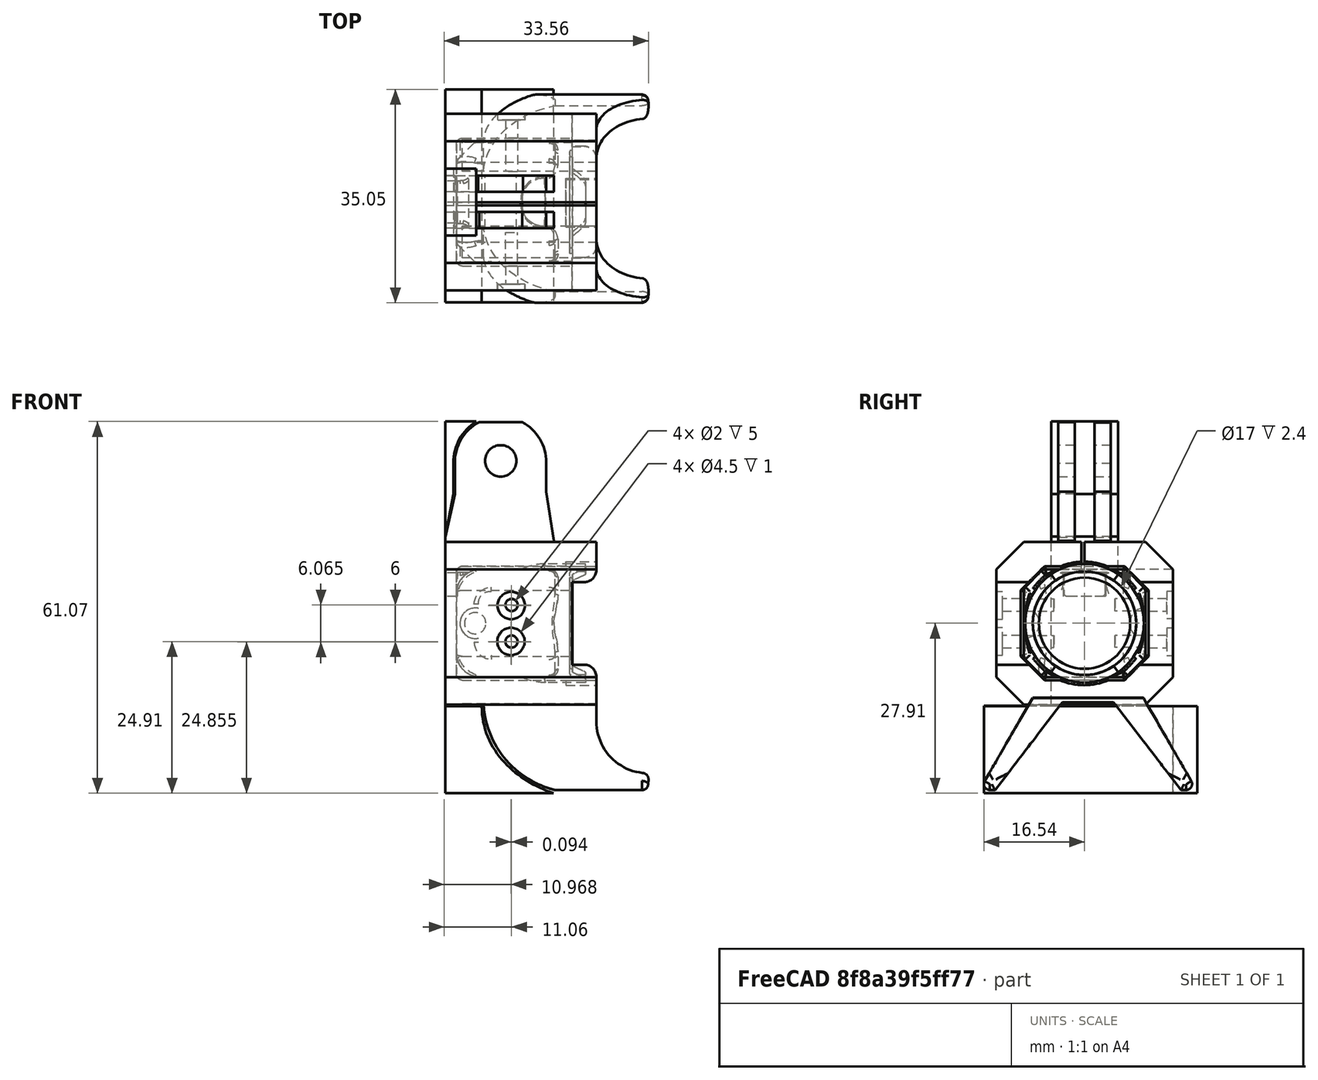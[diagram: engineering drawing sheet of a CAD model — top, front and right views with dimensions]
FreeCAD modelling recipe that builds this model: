
FCSTD DOCUMENT  (FreeCAD 0.19R24267 +99 (Git))
Label: O3头
License: All rights reserved
LicenseURL: http://en.wikipedia.org/wiki/All_rights_reserved
objects: Sketcher::SketchObject×22, PartDesign::Pocket×16, PartDesign::Pad×7, PartDesign::Fillet×5, Mesh::Feature×4, Part::Feature×1, PartDesign::Chamfer×1, PartDesign::Hole×1, PartDesign::Body×1
note: 84 computed .brp shape members not serialized (recipe doc carries the construction recipe); baked Part::Feature solids carry a one-line shape summary decoded from their .brp

FEATURE [Part::Feature] Solid  label="DJI_O3_CAM v1"
  shape: bbox 22.46 x 20.3 x 19.67 mm, 153 faces (baked)
FEATURE [Sketcher::SketchObject] Sketch
  FullyConstrained = false
  MapMode = 5
  Placement = pos=(0,0,0) rot=(0.57735,0.57735,0.57735;2.0944rad)
  Support = -> [YZ_Plane]
  sketch-geometry (18):
    g0: LineSegment StartX=-0.5 StartY=14.2836 StartZ=0 EndX=3.43199 EndY=18.2213 EndZ=0
    g1: LineSegment StartX=3.43199 StartY=18.2213 StartZ=0 EndX=16.5779 EndY=18.2213 EndZ=0
    g2: LineSegment StartX=16.5779 StartY=18.2213 StartZ=0 EndX=20.5092 EndY=14.283 EndZ=0
    g3: LineSegment StartX=20.5092 StartY=14.283 StartZ=0 EndX=20.5092 EndY=3.43765 EndZ=0
    g4: LineSegment StartX=20.5092 StartY=3.43765 StartZ=0 EndX=16.5772 EndY=-0.5 EndZ=0
    g5: LineSegment StartX=16.5772 StartY=-0.5 StartZ=0 EndX=3.43136 EndY=-0.5 EndZ=0
    g6: LineSegment StartX=3.43136 StartY=-0.5 StartZ=0 EndX=-0.5 EndY=3.43828 EndZ=0
    g7: LineSegment StartX=-0.5 StartY=3.43828 StartZ=0 EndX=-0.5 EndY=14.2836 EndZ=0
    g8: LineSegment StartX=0.297912 StartY=2.88402 StartZ=0 EndX=2.88412 EndY=0.293255 EndZ=0
    g9: LineSegment StartX=19.6882 StartY=2.88174 StartZ=0 EndX=17.0961 EndY=0.285953 EndZ=0
    g10: LineSegment StartX=3.7151 StartY=17.7213 StartZ=0 EndX=5.2908 EndY=17.7213 EndZ=0
    g11: LineSegment StartX=3.91307 StartY=0 StartZ=0 EndX=4.96058 EndY=0 EndZ=0
    g12: LineSegment StartX=20.0092 StartY=5.92573 StartZ=0 EndX=20.0092 EndY=3.95872 EndZ=0
    g13: LineSegment StartX=18.612 StartY=15.9146 StartZ=0 EndX=19.1853 EndY=15.3357 EndZ=0
    g14: LineSegment StartX=-4.5 StartY=22.2213 StartZ=0 EndX=24.5092 EndY=22.2213 EndZ=0
    g15: LineSegment StartX=24.5092 StartY=22.2213 StartZ=0 EndX=24.5092 EndY=-4.5 EndZ=0
    g16: LineSegment StartX=24.5092 StartY=-4.5 StartZ=0 EndX=-4.5 EndY=-4.5 EndZ=0
    g17: LineSegment StartX=-4.5 StartY=-4.5 StartZ=0 EndX=-4.5 EndY=22.2213 EndZ=0
  constraints (55):
    c: Coincident(g0,g1)
    c: Horizontal(g1)
    c: Coincident(g1,g2)
    c: Coincident(g2,g3)
    c: Vertical(g3)
    c: Coincident(g3,g4)
    c: Coincident(g4,g5)
    c: Horizontal(g5)
    c: Coincident(g5,g6)
    c: Coincident(g6,g7)
    c: Vertical(g7)
    c: Parallel(g4,g0)
    c: Parallel(g2,g6)
    c: Equal(g1,g5)
    c: Equal(g7,g3)
    c: Equal(g0,g2)
    c: Coincident(g7,g0)
    c: DistanceX(g8) = 0.297912
    c: DistanceY(g8) = 2.88402
    c: DistanceX(g8) = 2.88412
    c: DistanceY(g8) = 0.293255
    c: Parallel(g8,g6)
    c: DistanceX(g9,g9) = -2.59206
    c: DistanceY(g9,g9) = -2.59578
    c: Parallel(g4,g9)
    c: DistanceX(g-2,g0) = -0.5
    c: Horizontal(g10)
    c: DistanceX(g10,g10) = 1.5757
    c: DistanceX(g10) = 3.7151
    c: DistanceY(g10) = 17.7213
    c: PointOnObject(g11,g-1)
    c: PointOnObject(g11,g-1)
    c: Distance(g5,g11) = 0.5
    c: Vertical(g12)
    c: DistanceX(g12) = 20.0092
    c: DistanceY(g12) = 3.95872
    c: Distance(g3,g12) = 0.5
    c: DistanceX(g13,g13) = 0.573332
    c: DistanceY(g13,g13) = -0.578954
    c: Distance(g2,g13) = 0.2
    c: DistanceX(g13) = 19.1853
    c: DistanceY(g13) = 15.3357
    c: Coincident(g14,g15)
    c: Coincident(g15,g16)
    c: Coincident(g16,g17)
    c: Coincident(g17,g14)
    c: Horizontal(g14)
    c: Horizontal(g16)
    c: Vertical(g15)
    c: Vertical(g17)
    c: Distance(g2,g15) = 4
    c: Distance(g0,g17) = 4
    c: Distance(g0,g10) = 0.5
    c: Distance(g14,g1) = 4
    c: Distance(g15,g5) = 4
FEATURE [PartDesign::Pad] Pad
  Direction = (1,1,1)
  Length = 23
  Length2 = 100
  Placement = pos=(0,0,0) rot=(0.57735,0.57735,0.57735;2.0944rad)
  Profile = -> Sketch
  Type = 0
FEATURE [Sketcher::SketchObject] Sketch001
  ExternalGeometry = -> [Pad]
  FullyConstrained = false
  MapMode = 5
  Placement = pos=(0,0,0) rot=(0.57735,0.57735,-0.57735;4.18879rad)
  Support = -> [Pad]
  sketch-geometry (8):
    g0: LineSegment StartX=-4.5 StartY=4.5 StartZ=0 EndX=24.5092 EndY=4.5 EndZ=0
    g1: LineSegment StartX=24.5092 StartY=4.5 StartZ=0 EndX=24.5092 EndY=-22.2213 EndZ=0
    g2: LineSegment StartX=24.5092 StartY=-22.2213 StartZ=0 EndX=-4.5 EndY=-22.2213 EndZ=0
    g3: LineSegment StartX=-4.5 StartY=-22.2213 StartZ=0 EndX=-4.5 EndY=4.5 EndZ=0
    g4: LineSegment StartX=6.55538 StartY=-13.2436 StartZ=0 EndX=13.4769 EndY=-13.2436 EndZ=0
    g5: LineSegment StartX=13.4769 StartY=-13.2436 StartZ=0 EndX=13.4769 EndY=-17.1545 EndZ=0
    g6: LineSegment StartX=13.4769 StartY=-17.1545 StartZ=0 EndX=6.55538 EndY=-17.1545 EndZ=0
    g7: LineSegment StartX=6.55538 StartY=-17.1545 StartZ=0 EndX=6.55538 EndY=-13.2436 EndZ=0
  constraints (18):
    c: Coincident(g0,g1)
    c: Coincident(g1,g2)
    c: Coincident(g2,g3)
    c: Coincident(g3,g0)
    c: Horizontal(g0)
    c: Horizontal(g2)
    c: Vertical(g1)
    c: Vertical(g3)
    c: Coincident(g0,g-3)
    c: Coincident(g1,g-4)
    c: Coincident(g4,g5)
    c: Coincident(g5,g6)
    c: Coincident(g6,g7)
    c: Coincident(g7,g4)
    c: Horizontal(g4)
    c: Horizontal(g6)
    c: Vertical(g5)
    c: Vertical(g7)
FEATURE [PartDesign::Pad] Pad001
  BaseFeature = -> Pad
  Direction = (1,1,1)
  Length = 2
  Length2 = 100
  Placement = pos=(0,0,0) rot=(0.57735,0.57735,0.57735;2.0944rad)
  Profile = -> Sketch001
  Type = 0
FEATURE [Sketcher::SketchObject] Sketch002
  FullyConstrained = false
  MapMode = 5
  Placement = pos=(23,-5.1e-15,5.1e-15) rot=(0.57735,0.57735,0.57735;2.0944rad)
  Support = -> [Pad001]
  sketch-geometry (1):
    g0: Circle CenterX=9.92445 CenterY=8.8254 CenterZ=0 NormalX=0 NormalY=0 NormalZ=1 AngleXU=0 Radius=10.1445
FEATURE [PartDesign::Pocket] Pocket
  BaseFeature = -> Pad001
  Length = 5
  Length2 = 100
  Placement = pos=(0,0,0) rot=(0.57735,0.57735,0.57735;2.0944rad)
  Profile = -> Sketch002
  Type = 0
FEATURE [Sketcher::SketchObject] Sketch003
  FullyConstrained = false
  MapMode = 5
  Placement = pos=(23,-5.1e-15,5.1e-15) rot=(0.57735,0.57735,0.57735;2.0944rad)
  Support = -> [Pocket]
  sketch-geometry (4):
    g0: LineSegment StartX=-7.54895 StartY=15.6174 StartZ=0 EndX=32.5422 EndY=15.6174 EndZ=0
    g1: LineSegment StartX=32.5422 StartY=15.6174 StartZ=0 EndX=32.5422 EndY=2.04912 EndZ=0
    g2: LineSegment StartX=32.5422 StartY=2.04912 StartZ=0 EndX=-7.54895 EndY=2.04912 EndZ=0
    g3: LineSegment StartX=-7.54895 StartY=2.04912 StartZ=0 EndX=-7.54895 EndY=15.6174 EndZ=0
  constraints (8):
    c: Coincident(g0,g1)
    c: Coincident(g1,g2)
    c: Coincident(g2,g3)
    c: Coincident(g3,g0)
    c: Horizontal(g0)
    c: Horizontal(g2)
    c: Vertical(g1)
    c: Vertical(g3)
FEATURE [PartDesign::Pocket] Pocket001
  BaseFeature = -> Pocket
  Length = 4
  Length2 = 100
  Placement = pos=(0,0,0) rot=(0.57735,0.57735,0.57735;2.0944rad)
  Profile = -> Sketch003
  Type = 0
FEATURE [PartDesign::Chamfer] Chamfer
  Angle = 45
  Base = -> Pocket001 [Edge13,Edge2,Edge11,Edge1]
  BaseFeature = -> Pocket001
  ChamferType = 0
  FlipDirection = false
  Placement = pos=(0,0,0) rot=(0.57735,0.57735,0.57735;2.0944rad)
  Size = 4.5
  Size2 = 1
  SupportTransform = false
FEATURE [Sketcher::SketchObject] Sketch004
  FullyConstrained = false
  MapMode = 5
  Placement = pos=(23,-5.1e-15,5.1e-15) rot=(0.57735,0.57735,0.57735;2.0944rad)
  Support = -> [Chamfer]
  sketch-geometry (8):
    g0: LineSegment StartX=6.37015 StartY=-4.11848 StartZ=0 EndX=-4.6953 EndY=-18.5495 EndZ=0
    g1: LineSegment StartX=-4.6953 StartY=-18.5495 StartZ=0 EndX=-7.27173 EndY=-18.5495 EndZ=0
    g2: LineSegment StartX=-7.27173 StartY=-18.5495 StartZ=0 EndX=1.47566 EndY=-3.39858 EndZ=0
    g3: LineSegment StartX=1.47566 StartY=-3.39858 StartZ=0 EndX=19.6665 EndY=-3.39858 EndZ=0
    g4: LineSegment StartX=19.6665 StartY=-3.39858 StartZ=0 EndX=28.4139 EndY=-18.5495 EndZ=0
    g5: LineSegment StartX=28.4139 StartY=-18.5495 StartZ=0 EndX=25.8375 EndY=-18.5495 EndZ=0
    g6: LineSegment StartX=25.8375 StartY=-18.5495 StartZ=0 EndX=14.772 EndY=-4.11848 EndZ=0
    g7: LineSegment StartX=14.772 StartY=-4.11848 StartZ=0 EndX=6.37015 EndY=-4.11848 EndZ=0
  constraints (17):
    c: Coincident(g0,g1)
    c: Coincident(g1,g2)
    c: Coincident(g2,g3)
    c: Horizontal(g3)
    c: Coincident(g3,g4)
    c: Coincident(g4,g5)
    c: Coincident(g5,g6)
    c: Coincident(g6,g7)
    c: Horizontal(g7)
    c: Coincident(g0,g7)
    c: Equal(g0,g6)
    c: Equal(g2,g4)
    c: Equal(g1,g5)
    c: Horizontal(g1)
    c: Horizontal(g5)
    c: Angle(g-2,g2) = 2.61799
    c: Angle(g-2,g4) = 0.523599
FEATURE [PartDesign::Pad] Pad002
  BaseFeature = -> Chamfer
  Direction = (1,1,1)
  Length = 44
  Length2 = 100
  Midplane = true
  Placement = pos=(0,0,0) rot=(0.57735,0.57735,0.57735;2.0944rad)
  Profile = -> Sketch004
  Type = 0
FEATURE [Sketcher::SketchObject] Sketch005
  FullyConstrained = false
  MapMode = 5
  Placement = pos=(-2e-15,-4.5,1e-15) rot=(-0.57735,-0.57735,0.57735;4.18879rad)
  Support = -> [Pad002]
  sketch-geometry (12):
    g0: LineSegment StartX=3.10706 StartY=23.3142 StartZ=0 EndX=3.40969 EndY=23.0045 EndZ=0
    g1: LineSegment StartX=3.40969 StartY=23.0045 StartZ=0 EndX=4.50917 EndY=23.0045 EndZ=0
    g2: LineSegment StartX=4.50917 StartY=23.0045 StartZ=0 EndX=7.27153 EndY=23.0045 EndZ=0
    g3: ArcOfCircle CenterX=7.27153 CenterY=31.5281 CenterZ=0 NormalX=0 NormalY=0 NormalZ=1 AngleXU=0 Radius=8.52358 StartAngle=4.71239 EndAngle=6.29373
    g4: LineSegment StartX=15.7946 StartY=31.6179 StartZ=0 EndX=18.9819 EndY=31.4264 EndZ=0
    g5: LineSegment StartX=18.9819 StartY=31.4264 StartZ=0 EndX=18.9819 EndY=19.86 EndZ=0
    g6: ArcOfCircle CenterX=3.54244 CenterY=19.86 CenterZ=0 NormalX=0 NormalY=0 NormalZ=1 AngleXU=0 Radius=15.4394 StartAngle=4.77707 EndAngle=6.28319
    g7: LineSegment StartX=4.54036 StartY=4.45281 StartZ=0 EndX=4.54036 EndY=0.607622 EndZ=0
    g8: LineSegment StartX=4.54036 StartY=0.607622 StartZ=0 EndX=22.1043 EndY=0.607622 EndZ=0
    g9: LineSegment StartX=22.1043 StartY=0.607622 StartZ=0 EndX=19.9359 EndY=48.2984 EndZ=0
    g10: LineSegment StartX=19.9359 StartY=48.2984 StartZ=0 EndX=1.70533 EndY=46.4652 EndZ=0
    g11: LineSegment StartX=1.70533 StartY=46.4652 StartZ=0 EndX=3.10706 EndY=23.3142 EndZ=0
  constraints (16):
    c: Coincident(g0,g1)
    c: Horizontal(g1)
    c: Coincident(g1,g2)
    c: Horizontal(g2)
    c: Tangent(g2,g3) = -1.5708
    c: Coincident(g3,g4)
    c: Coincident(g4,g5)
    c: Vertical(g5)
    c: Tangent(g5,g6) = 1.5708
    c: Coincident(g6,g7)
    c: Coincident(g7,g8)
    c: Horizontal(g8)
    c: Coincident(g8,g9)
    c: Coincident(g9,g10)
    c: Coincident(g10,g11)
    c: Coincident(g11,g0)
FEATURE [PartDesign::Pocket] Pocket002
  BaseFeature = -> Pad002
  Length = 70
  Length2 = 100
  Midplane = true
  Placement = pos=(0,0,0) rot=(0.57735,0.57735,0.57735;2.0944rad)
  Profile = -> Sketch005
  Reversed = true
  Type = 0
FEATURE [Sketcher::SketchObject] Sketch006
  FullyConstrained = false
  MapMode = 5
  Placement = pos=(-6.2e-15,9.8e-15,22.2213) rot=(0,0,-1;1.5708rad)
  Support = -> [Pocket002]
  sketch-geometry (4):
    g0: LineSegment StartX=-9.49793 StartY=26.554 StartZ=0 EndX=-9.99793 EndY=26.554 EndZ=0
    g1: LineSegment StartX=-9.99793 StartY=26.554 StartZ=0 EndX=-9.99793 EndY=-5.18853 EndZ=0
    g2: LineSegment StartX=-9.99793 StartY=-5.18853 StartZ=0 EndX=-9.49793 EndY=-5.18853 EndZ=0
    g3: LineSegment StartX=-9.49793 StartY=-5.18853 StartZ=0 EndX=-9.49793 EndY=26.554 EndZ=0
  constraints (9):
    c: Coincident(g0,g1)
    c: Coincident(g1,g2)
    c: Coincident(g2,g3)
    c: Coincident(g3,g0)
    c: Horizontal(g0)
    c: Horizontal(g2)
    c: Vertical(g1)
    c: Vertical(g3)
    c: Distance(g0) = 0.5
FEATURE [PartDesign::Pocket] Pocket003
  BaseFeature = -> Pocket002
  Length = 5
  Length2 = 100
  Placement = pos=(0,0,0) rot=(0.57735,0.57735,0.57735;2.0944rad)
  Profile = -> Sketch006
  Type = 0
FEATURE [Sketcher::SketchObject] Sketch007
  FullyConstrained = false
  MapMode = 5
  Placement = pos=(-2e-15,-4.5,1e-15) rot=(-0.57735,-0.57735,0.57735;4.18879rad)
  Support = -> [Pocket003]
  sketch-geometry (2):
    g0: Circle CenterX=-11.8592 CenterY=9.07199 CenterZ=0 NormalX=0 NormalY=0 NormalZ=1 AngleXU=0 Radius=1
    g1: Circle CenterX=-5.84964 CenterY=9.05821 CenterZ=0 NormalX=0 NormalY=0 NormalZ=1 AngleXU=0 Radius=1
  constraints (2):
    c: Diameter(g0) = 2
    c: Diameter(g1) = 2
FEATURE [PartDesign::Pocket] Pocket004
  BaseFeature = -> Pocket003
  Length = 90
  Length2 = 100
  Placement = pos=(0,0,0) rot=(0.57735,0.57735,0.57735;2.0944rad)
  Profile = -> Sketch007
  Type = 0
FEATURE [Sketcher::SketchObject] Sketch008
  FullyConstrained = false
  MapMode = 5
  Placement = pos=(-2e-15,-4.5,1e-15) rot=(-0.57735,-0.57735,0.57735;4.18879rad)
  Support = -> [Pocket004]
  sketch-geometry (2):
    g0: Circle CenterX=-11.7651 CenterY=9.01139 CenterZ=0 NormalX=0 NormalY=0 NormalZ=1 AngleXU=0 Radius=2.25
    g1: Circle CenterX=-5.86693 CenterY=8.96784 CenterZ=0 NormalX=0 NormalY=0 NormalZ=1 AngleXU=0 Radius=2.25
  constraints (2):
    c: Diameter(g0) = 4.5
    c: Diameter(g1) = 4.5
FEATURE [PartDesign::Pocket] Pocket005
  BaseFeature = -> Pocket004
  Length = 1
  Length2 = 100
  Placement = pos=(0,0,0) rot=(0.57735,0.57735,0.57735;2.0944rad)
  Profile = -> Sketch008
  Type = 0
FEATURE [Sketcher::SketchObject] Sketch009
  FullyConstrained = false
  MapMode = 5
  Placement = pos=(1.08e-14,24.5092,-5.4e-15) rot=(0.57735,0.57735,0.57735;4.18879rad)
  Support = -> [Pocket005]
  sketch-geometry (2):
    g0: Circle CenterX=5.80449 CenterY=9.03873 CenterZ=0 NormalX=0 NormalY=0 NormalZ=1 AngleXU=0 Radius=2.25
    g1: Circle CenterX=11.8697 CenterY=9.06153 CenterZ=0 NormalX=0 NormalY=0 NormalZ=1 AngleXU=0 Radius=2.25
  constraints (2):
    c: Diameter(g0) = 4.5
    c: Equal(g1,g0)
FEATURE [PartDesign::Pocket] Pocket006
  BaseFeature = -> Pocket005
  Length = 1
  Length2 = 100
  Placement = pos=(0,0,0) rot=(0.57735,0.57735,0.57735;2.0944rad)
  Profile = -> Sketch009
  Type = 0
FEATURE [PartDesign::Fillet] Fillet
  Base = -> Pocket006 [Edge131,Edge129,Edge141,Edge16]
  BaseFeature = -> Pocket006
  Placement = pos=(0,0,0) rot=(0.57735,0.57735,0.57735;2.0944rad)
  Radius = 2
  SupportTransform = false
FEATURE [PartDesign::Fillet] Fillet001
  Base = -> Fillet [Edge149,Edge128]
  BaseFeature = -> Fillet
  Placement = pos=(0,0,0) rot=(0.57735,0.57735,0.57735;2.0944rad)
  Radius = 1
  SupportTransform = false
FEATURE [Sketcher::SketchObject] Sketch010
  FullyConstrained = true
  MapMode = 5
  Placement = pos=(-6.2e-15,9.8e-15,22.2213) rot=(0,0,-1;1.5708rad)
  Support = -> [Fillet001]
FEATURE [Mesh::Feature] GEPRCMK5PIGTAIL
FEATURE [Mesh::Feature] geprc_mark5GEP_MK5_gopro_mount  label="geprc_mark5GEP-MK5_gopro_mount"
  Placement = pos=(-51,10,66) rot=(0.57735,-0.57735,0.57735;2.0944rad)
FEATURE [Sketcher::SketchObject] Sketch011
  FullyConstrained = false
  MapMode = 5
  Placement = pos=(-2,9e-16,-9e-16) rot=(0.57735,0.57735,-0.57735;4.18879rad)
  Support = -> [Fillet001]
  sketch-geometry (8):
    g0: LineSegment StartX=5.70248 StartY=-21.8264 StartZ=0 EndX=8.37393 EndY=-21.8264 EndZ=0
    g1: LineSegment StartX=8.37393 StartY=-21.8264 StartZ=0 EndX=8.37393 EndY=-41.9091 EndZ=0
    g2: LineSegment StartX=8.37393 StartY=-41.9091 StartZ=0 EndX=5.70248 EndY=-41.9091 EndZ=0
    g3: LineSegment StartX=5.70248 StartY=-41.9091 StartZ=0 EndX=5.70248 EndY=-21.8264 EndZ=0
    g4: LineSegment StartX=11.6603 StartY=-21.832 StartZ=0 EndX=14.3317 EndY=-21.832 EndZ=0
    g5: LineSegment StartX=14.3317 StartY=-21.832 StartZ=0 EndX=14.3317 EndY=-41.814 EndZ=0
    g6: LineSegment StartX=14.3317 StartY=-41.814 StartZ=0 EndX=11.6603 EndY=-41.814 EndZ=0
    g7: LineSegment StartX=11.6603 StartY=-41.814 StartZ=0 EndX=11.6603 EndY=-21.832 EndZ=0
  constraints (16):
    c: Coincident(g0,g1)
    c: Coincident(g1,g2)
    c: Coincident(g2,g3)
    c: Coincident(g3,g0)
    c: Horizontal(g0)
    c: Horizontal(g2)
    c: Vertical(g1)
    c: Vertical(g3)
    c: Coincident(g4,g5)
    c: Coincident(g5,g6)
    c: Coincident(g6,g7)
    c: Coincident(g7,g4)
    c: Horizontal(g4)
    c: Horizontal(g6)
    c: Vertical(g5)
    c: Vertical(g7)
FEATURE [PartDesign::Pad] Pad003
  BaseFeature = -> Fillet001
  Direction = (1,1,1)
  Length = 18
  Length2 = 100
  Placement = pos=(0,0,0) rot=(0.57735,0.57735,0.57735;2.0944rad)
  Profile = -> Sketch011
  Reversed = true
  Type = 0
FEATURE [Sketcher::SketchObject] Sketch012
  FullyConstrained = false
  MapMode = 5
  Placement = pos=(3.81e-14,14.3317,-9e-16) rot=(0.57735,0.57735,0.57735;4.18879rad)
  Support = -> [Pad003]
  sketch-geometry (11):
    g0: LineSegment StartX=22.2256 StartY=16.0321 StartZ=0 EndX=30.4473 EndY=14.7877 EndZ=0
    g1: LineSegment StartX=30.4473 StartY=14.7877 StartZ=0 EndX=35.2587 EndY=14.7877 EndZ=0
    g2: ArcOfCircle CenterX=35.2587 CenterY=7.26172 CenterZ=0 NormalX=0 NormalY=0 NormalZ=1 AngleXU=0 Radius=7.526 StartAngle=4.6959 EndAngle=7.85398
    g3: LineSegment StartX=35.1346 StartY=-0.263258 StartZ=0 EndX=30.096 EndY=-0.263258 EndZ=0
    g4: LineSegment StartX=30.096 StartY=-0.263258 StartZ=0 EndX=22.1815 EndY=-2.01839 EndZ=0
    g5: LineSegment StartX=22.1815 StartY=-2.01839 StartZ=0 EndX=39.8338 EndY=-4.45021 EndZ=0
    g6: LineSegment StartX=39.8338 StartY=-4.45021 StartZ=0 EndX=43.8849 EndY=-2.81555 EndZ=0
    g7: LineSegment StartX=43.8849 StartY=-2.81555 StartZ=0 EndX=43.8849 EndY=16.445 EndZ=0
    g8: LineSegment StartX=43.8849 StartY=16.445 StartZ=0 EndX=23.3499 EndY=17.3656 EndZ=0
    g9: LineSegment StartX=23.3499 StartY=17.3656 StartZ=0 EndX=22.2256 EndY=16.0321 EndZ=0
    g10: Circle CenterX=35.5458 CenterY=7.28339 CenterZ=0 NormalX=0 NormalY=0 NormalZ=1 AngleXU=0 Radius=2.57939
  constraints (13):
    c: Coincident(g0,g1)
    c: Horizontal(g1)
    c: Tangent(g1,g2) = 1.5708
    c: Coincident(g2,g3)
    c: Horizontal(g3)
    c: Coincident(g3,g4)
    c: Coincident(g4,g5)
    c: Coincident(g5,g6)
    c: Coincident(g6,g7)
    c: Vertical(g7)
    c: Coincident(g7,g8)
    c: Coincident(g8,g9)
    c: Coincident(g9,g0)
FEATURE [PartDesign::Pocket] Pocket007
  BaseFeature = -> Pad003
  Length = 13
  Length2 = 100
  Placement = pos=(0,0,0) rot=(0.57735,0.57735,0.57735;2.0944rad)
  Profile = -> Sketch012
  Type = 0
FEATURE [Sketcher::SketchObject] Sketch013
  FullyConstrained = false
  MapMode = 5
  Placement = pos=(1.08e-14,24.5092,-5.4e-15) rot=(0.57735,0.57735,0.57735;4.18879rad)
  Support = -> [Pocket007]
  sketch-geometry (11):
    g0: LineSegment StartX=-19.0484 StartY=15.974 StartZ=0 EndX=-19.0484 EndY=-2 EndZ=0
    g1: ArcOfCircle CenterX=-4.68956 CenterY=17.6568 CenterZ=0 NormalX=0 NormalY=0 NormalZ=1 AngleXU=0 Radius=13.4905 StartAngle=3.94593 EndAngle=4.705
    g2: ArcOfCircle CenterX=-0.649848 CenterY=21.8525 CenterZ=0 NormalX=0 NormalY=0 NormalZ=1 AngleXU=0 Radius=19.3148 StartAngle=3.45085 EndAngle=3.94593
    g3: LineSegment StartX=42.0213 StartY=3.23392 StartZ=0 EndX=42.0213 EndY=-2 EndZ=0
    g4: LineSegment StartX=23.1025 StartY=-1.84436 StartZ=0 EndX=30.1009 EndY=-0.504038 EndZ=0
    g5: LineSegment StartX=30.1009 StartY=-0.504038 StartZ=0 EndX=35.2051 EndY=-0.504038 EndZ=0
    g6: ArcOfCircle CenterX=35.2051 CenterY=7.57959 CenterZ=0 NormalX=0 NormalY=0 NormalZ=1 AngleXU=0 Radius=8.08363 StartAngle=4.71239 EndAngle=5.71561
    g7: LineSegment StartX=-19.0484 StartY=-2 StartZ=0 EndX=42.0213 EndY=-2 EndZ=0
    g8: LineSegment StartX=-4.7892 StartY=4.16671 StartZ=0 EndX=-4.74934 EndY=4.16641 EndZ=0
    g9: LineSegment StartX=-4.74934 StartY=4.16641 StartZ=0 EndX=-4.74934 EndY=-1.84436 EndZ=0
    g10: LineSegment StartX=-4.74934 StartY=-1.84436 StartZ=0 EndX=23.1025 EndY=-1.84436 EndZ=0
  constraints (17):
    c: Vertical(g0)
    c: Tangent(g1,g2) = -1.5708
    c: Coincident(g2,g0)
    c: Vertical(g3)
    c: Coincident(g4,g5)
    c: Horizontal(g5)
    c: Tangent(g5,g6) = -1.5708
    c: Coincident(g6,g3)
    c: Coincident(g0,g7)
    c: Coincident(g7,g3)
    c: Horizontal(g7)
    c: Tangent(g1,g8) = -1.5708
    c: Coincident(g8,g9)
    c: Vertical(g9)
    c: Coincident(g9,g10)
    c: Coincident(g10,g4)
    c: Horizontal(g10)
FEATURE [PartDesign::Pad] Pad004
  BaseFeature = -> Pocket007
  Direction = (1,1,1)
  Length = 31
  Length2 = 100
  Placement = pos=(0,0,0) rot=(0.57735,0.57735,0.57735;2.0944rad)
  Profile = -> Sketch013
  Reversed = true
  Type = 0
FEATURE [PartDesign::Pad] Pad005
  BaseFeature = -> Pad004
  Direction = (1,1,1)
  Length = 4
  Length2 = 100
  Placement = pos=(0,0,0) rot=(0.57735,0.57735,0.57735;2.0944rad)
  Profile = -> Pad004 [Face64]
  Type = 0
FEATURE [PartDesign::Pocket] Pocket008
  BaseFeature = -> Pad005
  Length = 11
  Length2 = 100
  Placement = pos=(0,0,0) rot=(0.57735,0.57735,0.57735;2.0944rad)
  Profile = -> Pad005 [Face82]
  Type = 0
FEATURE [PartDesign::Pocket] Pocket009
  BaseFeature = -> Pocket008
  Length = 9
  Length2 = 100
  Placement = pos=(0,0,0) rot=(0.57735,0.57735,0.57735;2.0944rad)
  Profile = -> Pocket008 [Face111]
  Type = 0
FEATURE [Sketcher::SketchObject] Sketch014
  FullyConstrained = true
  MapMode = 5
  Placement = pos=(2.6e-15,4.50921,-1.82e-14) rot=(0.57735,0.57735,-0.57735;2.0944rad)
  Support = -> [Pocket009]
FEATURE [Sketcher::SketchObject] Sketch015
  ExternalGeometry = -> [Pocket009]
  FullyConstrained = true
  MapMode = 5
  Placement = pos=(2.6e-15,4.50921,-1.82e-14) rot=(0.57735,0.57735,-0.57735;2.0944rad)
  Support = -> [Pocket009]
FEATURE [Sketcher::SketchObject] Sketch016
  FullyConstrained = false
  MapMode = 5
  Placement = pos=(2.6e-15,4.50921,-1.82e-14) rot=(0.57735,0.57735,-0.57735;2.0944rad)
  Support = -> [Pocket009]
  sketch-geometry (4):
    g0: LineSegment StartX=4.62319 StartY=-1.73688 StartZ=0 EndX=4.70056 EndY=-1.73688 EndZ=0
    g1: LineSegment StartX=4.70056 StartY=-1.73688 StartZ=0 EndX=4.70056 EndY=-2.31716 EndZ=0
    g2: LineSegment StartX=4.70056 StartY=-2.31716 StartZ=0 EndX=4.62319 EndY=-2.31716 EndZ=0
    g3: LineSegment StartX=4.62319 StartY=-2.31716 StartZ=0 EndX=4.62319 EndY=-1.73688 EndZ=0
  constraints (8):
    c: Coincident(g0,g1)
    c: Coincident(g1,g2)
    c: Coincident(g2,g3)
    c: Coincident(g3,g0)
    c: Horizontal(g0)
    c: Horizontal(g2)
    c: Vertical(g1)
    c: Vertical(g3)
FEATURE [PartDesign::Pocket] Pocket010
  BaseFeature = -> Pocket009
  Length = 0.1
  Length2 = 100
  Placement = pos=(0,0,0) rot=(0.57735,0.57735,0.57735;2.0944rad)
  Profile = -> Sketch016
  Type = 0
FEATURE [PartDesign::Pad] Pad006
  BaseFeature = -> Pocket010
  Direction = (1,1,1)
  Length = 11
  Length2 = 100
  Placement = pos=(0,0,0) rot=(0.57735,0.57735,0.57735;2.0944rad)
  Profile = -> Pocket010 [Face70]
  Type = 0
FEATURE [Sketcher::SketchObject] Sketch017
  FullyConstrained = false
  MapMode = 5
  Placement = pos=(-1.84437,9e-16,-4e-16) rot=(0.57735,0.57735,0.57735;2.0944rad)
  Support = -> [Pad006]
  sketch-geometry (6):
    g0: LineSegment StartX=25.0511 StartY=0.390689 StartZ=0 EndX=24.5152 EndY=-1e-16 EndZ=0
    g1: LineSegment StartX=24.5152 StartY=0 StartZ=0 EndX=20.2153 EndY=-4.32422 EndZ=0
    g2: LineSegment StartX=20.2153 StartY=-4.32422 StartZ=0 EndX=20.4634 EndY=-4.74125 EndZ=0
    g3: LineSegment StartX=20.4634 StartY=-4.74125 StartZ=0 EndX=28.7936 EndY=-4.74125 EndZ=0
    g4: LineSegment StartX=28.7936 StartY=-4.74125 StartZ=0 EndX=30.4142 EndY=0.390689 EndZ=0
    g5: LineSegment StartX=30.4142 StartY=0.390689 StartZ=0 EndX=25.0511 EndY=0.390689 EndZ=0
  constraints (9):
    c: PointOnObject(g0,g-1)
    c: Coincident(g0,g1)
    c: Coincident(g1,g2)
    c: Coincident(g2,g3)
    c: Horizontal(g3)
    c: Coincident(g3,g4)
    c: Coincident(g4,g5)
    c: Coincident(g5,g0)
    c: Horizontal(g5)
FEATURE [PartDesign::Pocket] Pocket011
  BaseFeature = -> Pad006
  Length = 5
  Length2 = 100
  Placement = pos=(0,0,0) rot=(0.57735,0.57735,0.57735;2.0944rad)
  Profile = -> Sketch017
  Type = 0
FEATURE [Sketcher::SketchObject] Sketch018
  FullyConstrained = false
  MapMode = 5
  Placement = pos=(-3e-15,-4.5,0) rot=(0.57735,0.57735,-0.57735;2.0944rad)
  Support = -> [Pocket011]
  sketch-geometry (4):
    g0: LineSegment StartX=-43.5155 StartY=-1.74474 StartZ=0 EndX=21.2568 EndY=-1.74474 EndZ=0
    g1: LineSegment StartX=21.2568 StartY=-1.74474 StartZ=0 EndX=21.2568 EndY=-4.02482 EndZ=0
    g2: LineSegment StartX=21.2568 StartY=-4.02482 StartZ=0 EndX=-43.5155 EndY=-4.02482 EndZ=0
    g3: LineSegment StartX=-43.5155 StartY=-4.02482 StartZ=0 EndX=-43.5155 EndY=-1.74474 EndZ=0
  constraints (8):
    c: Coincident(g0,g1)
    c: Coincident(g1,g2)
    c: Coincident(g2,g3)
    c: Coincident(g3,g0)
    c: Horizontal(g0)
    c: Horizontal(g2)
    c: Vertical(g1)
    c: Vertical(g3)
FEATURE [PartDesign::Hole] Hole
  BaseFeature = -> Pocket011
  Depth = 25
  DepthType = 0
  Diameter = 6
  DrillForDepth = false
  DrillPoint = 1
  DrillPointAngle = 118
  HoleCutCountersinkAngle = 90
  HoleCutCustomValues = false
  HoleCutDepth = 0
  HoleCutDiameter = 6.1
  HoleCutType = 0
  ModelActualThread = false
  Placement = pos=(0,0,0) rot=(0.57735,0.57735,0.57735;2.0944rad)
  Profile = -> Sketch018
  Tapered = false
  TaperedAngle = 90
  ThreadAngle = 0
  ThreadClass = 0
  ThreadCutOffInner = 0
  ThreadCutOffOuter = 0
  ThreadDirection = 0
  ThreadFit = 0
  ThreadPitch = 0
  ThreadSize = 0
  ThreadType = 0
  Threaded = false
FEATURE [Sketcher::SketchObject] Sketch019
  FullyConstrained = false
  MapMode = 5
  Placement = pos=(1.64e-14,24.5092,0) rot=(0.57735,0.57735,0.57735;4.18879rad)
  Support = -> [Hole]
  sketch-geometry (4):
    g0: LineSegment StartX=-19.7065 StartY=-1.84509 StartZ=0 EndX=44.5512 EndY=-1.84509 EndZ=0
    g1: LineSegment StartX=44.5512 StartY=-1.84509 StartZ=0 EndX=44.5512 EndY=-4.94766 EndZ=0
    g2: LineSegment StartX=44.5512 StartY=-4.94766 StartZ=0 EndX=-19.7065 EndY=-4.94766 EndZ=0
    g3: LineSegment StartX=-19.7065 StartY=-4.94766 StartZ=0 EndX=-19.7065 EndY=-1.84509 EndZ=0
  constraints (8):
    c: Coincident(g0,g1)
    c: Coincident(g1,g2)
    c: Coincident(g2,g3)
    c: Coincident(g3,g0)
    c: Horizontal(g0)
    c: Horizontal(g2)
    c: Vertical(g1)
    c: Vertical(g3)
FEATURE [PartDesign::Pocket] Pocket012
  BaseFeature = -> Hole
  Length = 33
  Length2 = 100
  Placement = pos=(0,0,0) rot=(0.57735,0.57735,0.57735;2.0944rad)
  Profile = -> Sketch019
  Type = 0
FEATURE [Sketcher::SketchObject] Sketch020
  FullyConstrained = false
  MapMode = 5
  Placement = pos=(1.4e-14,24.5092,-1.402e-13) rot=(0.57735,0.57735,-0.57735;2.0944rad)
  Support = -> [Pocket012]
  sketch-geometry (4):
    g0: LineSegment StartX=4.70013 StartY=-1.84466 StartZ=0 EndX=22.0687 EndY=-1.84466 EndZ=0
    g1: LineSegment StartX=22.0687 StartY=-1.84466 StartZ=0 EndX=22.0687 EndY=-3.23405 EndZ=0
    g2: LineSegment StartX=22.0687 StartY=-3.23405 StartZ=0 EndX=4.70013 EndY=-3.23405 EndZ=0
    g3: LineSegment StartX=4.70013 StartY=-3.23405 StartZ=0 EndX=4.70013 EndY=-1.84466 EndZ=0
  constraints (8):
    c: Coincident(g0,g1)
    c: Coincident(g1,g2)
    c: Coincident(g2,g3)
    c: Coincident(g3,g0)
    c: Horizontal(g0)
    c: Horizontal(g2)
    c: Vertical(g1)
    c: Vertical(g3)
FEATURE [Mesh::Feature] GEPRC_MK5_BODYBN220_SMA_T  label="GEPRC-MK5-BODYBN220+SMA+T"
  Placement = pos=(0,46.3,0) rot=(0,0,1;0rad)
FEATURE [Mesh::Feature] O3_________  label="O3天空端"
  Placement = pos=(-20.55,0,0) rot=(0,0,1;0rad)
FEATURE [PartDesign::Pocket] Pocket013
  BaseFeature = -> Pocket012
  Length = 14
  Length2 = 100
  Placement = pos=(0,0,0) rot=(0.57735,0.57735,0.57735;2.0944rad)
  Profile = -> Sketch020
  Type = 0
FEATURE [PartDesign::Pocket] Pocket014
  BaseFeature = -> Pocket013
  Length = 5
  Length2 = 100
  Placement = pos=(0,0,0) rot=(0.57735,0.57735,0.57735;2.0944rad)
  Profile = -> Pocket013 [Face130]
  Type = 0
FEATURE [PartDesign::Pocket] Pocket015
  BaseFeature = -> Pocket014
  Length = 3
  Length2 = 100
  Placement = pos=(0,0,0) rot=(0.57735,0.57735,0.57735;2.0944rad)
  Profile = -> Pocket014 [Face88]
  Type = 0
FEATURE [PartDesign::Fillet] Fillet002
  Base = -> Pocket015 [Edge180,Edge179,Edge178,Edge87,Edge84,Edge104,Edge166,Edge167,Edge168]
  BaseFeature = -> Pocket015
  Placement = pos=(0,0,0) rot=(0.57735,0.57735,0.57735;2.0944rad)
  Radius = 1
  SupportTransform = false
FEATURE [PartDesign::Fillet] Fillet003
  Base = -> Fillet002 [Face60]
  BaseFeature = -> Fillet002
  Placement = pos=(0,0,0) rot=(0.57735,0.57735,0.57735;2.0944rad)
  Radius = 1
  SupportTransform = false
FEATURE [PartDesign::Fillet] Fillet004
  Base = -> Fillet003 [Face39]
  BaseFeature = -> Fillet003
  Placement = pos=(0,0,0) rot=(0.57735,0.57735,0.57735;2.0944rad)
  Radius = 1
  SupportTransform = false
FEATURE [Sketcher::SketchObject] Sketch021
  FullyConstrained = false
  MapMode = 5
  Support = -> [XY_Plane]
  sketch-geometry (4):
    g0: Circle CenterX=-12.246 CenterY=46.2936 CenterZ=0 NormalX=0 NormalY=0 NormalZ=1 AngleXU=0 Radius=2.5
    g1: Circle CenterX=12.2377 CenterY=46.2817 CenterZ=0 NormalX=0 NormalY=0 NormalZ=1 AngleXU=0 Radius=2.5
    g2: Circle CenterX=14.2878 CenterY=-4.70545 CenterZ=0 NormalX=0 NormalY=0 NormalZ=1 AngleXU=0 Radius=2.5
    g3: Circle CenterX=-14.2417 CenterY=-4.6915 CenterZ=0 NormalX=0 NormalY=0 NormalZ=1 AngleXU=0 Radius=2.5
  constraints (8):
    c: Diameter(g0) = 5
    c: Equal(g0,g1) = 5
    c: DistanceX(g0,g2) = 26.5337
    c: DistanceY(g0,g2) = -50.9991
    c: DistanceX(g1,g2) = 2.05005
    c: DistanceY(g1,g2) = -50.9871
    c: DistanceX(g3,g2) = 28.5295
    c: DistanceY(g3,g2) = -0.013955
FEATURE [PartDesign::Body] Body
  Group = -> [Sketch,Pad,Sketch001,Pad001,Sketch002,Pocket,Sketch003,Pocket001,Chamfer,Sketch004,Pad002,Sketch005,Pocket002,Sketch006,Pocket003,Sketch007,Pocket004,Sketch008,Pocket005,Sketch009,Pocket006,Fillet,Fillet001,Sketch010,Sketch011,Pad003,Sketch012,Pocket007,Sketch013,Pad004,Pad005,Pocket008,Pocket009,Sketch014,Sketch015,Sketch016,Pocket010,Pad006,Sketch017,Pocket011,Sketch018,Hole,Sketch019,Pocket012,+8 more]
  Origin = -> Origin
  Tip = -> Fillet004
